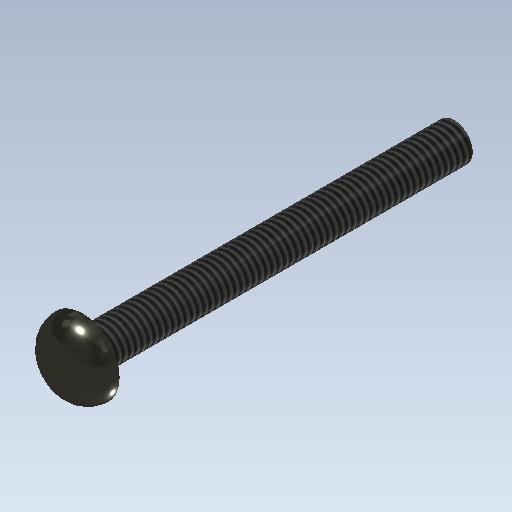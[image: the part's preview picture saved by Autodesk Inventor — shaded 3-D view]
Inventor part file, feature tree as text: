
AUTODESK INVENTOR PART (.ipt)
format: ipt  version: 2020.2 (Build 242310000, 310)  size: 155,136 bytes
history: native  units: mm
features: extrude x4, sketch x4, other x1, fillet x1, thread x1
ambient origin geometry x1: Origin
bodies: Body1 (feature_tree)
feature tree (11):
  other  "ソリッド1"
  extrude  "押し出し1"  Depth=3.0mm
  extrude  "押し出し2"  Depth=6.0mm TaperAngle=0.0deg
  fillet  "フィレット1"  Radius=6.0mm
  thread  "ねじ1"
  extrude  "押し出し3"  Depth=2.0mm TaperAngle=0.0deg
  extrude  "押し出し4"  Depth=2.0mm
  sketch  "スケッチ1"
  sketch  "スケッチ2"
  sketch  "スケッチ3"
  sketch  "スケッチ4"
